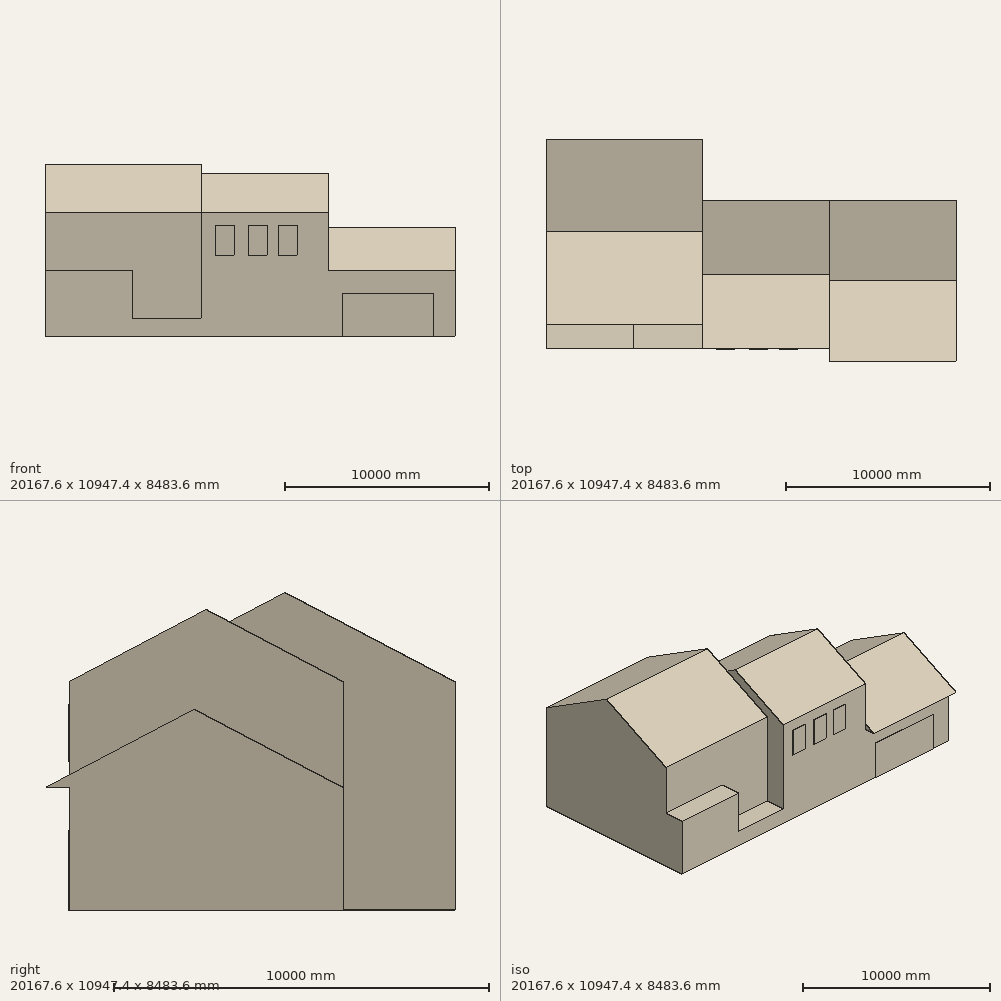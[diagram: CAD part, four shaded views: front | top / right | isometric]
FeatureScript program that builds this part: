
annotation { "Feature Type Name" : "Feature", "Feature Type Description" : "" }
export const myFeature = defineFeature(function(context is Context, id is Id, definition is map)
    precondition{}
    {
        {
            var Q0;
            Q0=qCreatedBy(makeId("Right.planeOp"),FACE);
            cPlane(context, id + "F0", {"entities" : qUnion([Q0]), "cplaneType" : CPlaneType.OFFSET, "offset" : 6248.4 * mm, "width" : 152.4 * mm, "height" : 152.4 * mm});
        }
        {
            var Q0;
            Q0=qCreatedBy(makeId("Right.planeOp"),FACE);
            cPlane(context, id + "F1", {"entities" : qUnion([Q0]), "cplaneType" : CPlaneType.OFFSET, "offset" : 7670.8 * mm, "oppositeDirection" : true, "width" : 152.4 * mm, "height" : 152.4 * mm});
        }
        {
            var Q0;
            Q0=qCreatedBy(id+"F0.planeOp",FACE);
            var sketch = newSketch(context, id + "F2", { "sketchPlane" : qUnion([Q0])});
            skLineSegment(sketch, "E0", {"start": v(0, 0) * mm, "end": v(7315.2, 0) * mm});
            skLineSegment(sketch, "E1.0", {"start": v(7315.2, 0) * mm, "end": v(7315.2, 6.35) * mm});
            skLineSegment(sketch, "E2.MirrorCS", {"start": v(3657.6, 8030.48) * mm, "end": v(7315.2, 6102.35) * mm});
            skLineSegment(sketch, "E3.0", {"start": v(0, 6.35) * mm, "end": v(7315.2, 6.35) * mm});
            skLineSegment(sketch, "E4", {"start": v(0, 6.35) * mm, "end": v(0, 6102.35) * mm});
            skLineSegment(sketch, "E5.trimOffspring", {"start": v(7315.2, 6.35) * mm, "end": v(7315.2, 6102.35) * mm});
            skLineSegment(sketch, "E6.MirrorCS", {"start": v(3657.6, 8030.48) * mm, "end": v(0, 6102.35) * mm});
            skSolve(sketch);
        }
        {
            var Q0;
            Q0=qCreatedBy(makeId("Right.planeOp"),FACE);
            var sketch = newSketch(context, id + "F3", { "sketchPlane" : qUnion([Q0])});
            skLineSegment(sketch, "E7", {"start": v(0, 0) * mm, "end": v(10312.4, 0) * mm});
            skLineSegment(sketch, "E8.0", {"start": v(0, 914.4) * mm, "end": v(1219.2, 914.4) * mm});
            skLineSegment(sketch, "E9.0", {"start": v(1219.2, 914.4) * mm, "end": v(1219.2, 6096) * mm});
            skLineSegment(sketch, "E10.0", {"start": v(10312.4, 0) * mm, "end": v(10312.4, 6096) * mm});
            skLineSegment(sketch, "E11", {"start": v(1219.2, 6096) * mm, "end": v(5765.8, 8483.6) * mm});
            skLineSegment(sketch, "E12", {"start": v(5765.8, 8483.6) * mm, "end": v(10312.4, 6096) * mm});
            skLineSegment(sketch, "E13", {"start": v(0, 0) * mm, "end": v(0, 914.4) * mm});
            skLineSegment(sketch, "E14.0", {"start": v(0, 6.35) * mm, "end": v(10312.4, 6.35) * mm});
            skLineSegment(sketch, "E15.0", {"start": v(0, 12.7) * mm, "end": v(10312.4, 12.7) * mm});
            skSolve(sketch);
        }
        {
            var Q0;
            Q0=qCreatedBy(id+"F1.planeOp",FACE);
            var sketch = newSketch(context, id + "F4", { "sketchPlane" : qUnion([Q0])});
            skLineSegment(sketch, "E16", {"start": v(0, 0) * mm, "end": v(10312.4, 0) * mm});
            skLineSegment(sketch, "E17", {"start": v(0, 0) * mm, "end": v(0, 3276.6) * mm});
            skLineSegment(sketch, "E18.0", {"start": v(10312.4, 0) * mm, "end": v(10312.4, 6096) * mm});
            skLineSegment(sketch, "E19.0", {"start": v(0, 3276.6) * mm, "end": v(1219.2, 3276.6) * mm});
            skLineSegment(sketch, "E20.0", {"start": v(1219.2, 3276.6) * mm, "end": v(1219.2, 6096) * mm});
            skLineSegment(sketch, "E21", {"start": v(1219.2, 6096) * mm, "end": v(5765.8, 8483.6) * mm});
            skLineSegment(sketch, "E22", {"start": v(10312.4, 6096) * mm, "end": v(5765.8, 8483.6) * mm});
            skSolve(sketch);
        }
        {
            var Q0;
            Q0=qCreatedBy(makeId("Right.planeOp"),FACE);
            cPlane(context, id + "F5", {"entities" : qUnion([Q0]), "cplaneType" : CPlaneType.OFFSET, "offset" : 6705.6 * mm, "width" : 152.4 * mm, "height" : 152.4 * mm});
        }
        {
            var Q0;
            Q0=qCreatedBy(makeId("Right.planeOp"),FACE);
            cPlane(context, id + "F6", {"entities" : qUnion([Q0]), "cplaneType" : CPlaneType.OFFSET, "offset" : 8128 * mm, "oppositeDirection" : true, "width" : 152.4 * mm, "height" : 152.4 * mm});
        }
        {
            var Q0;
            Q0=makeQuery(id+"F4.imprint","IMPRINT",FACE,{"disambiguationData":[TD([[makeQuery(id+"F4.imprint","IMPRINT",EDGE,{"derivedFrom":sQuery(id+"F4.wireOp",EDGE,"E16")}),1.0]])]});
            extrude(context, id + "F7", {"entities" : qUnion([Q0]), "depth" : 4267.2 * mm});
        }
        {
            var Q0;
            {var subQ0=sQuery(id+"F3.wireOp",EDGE,"E8.0");Q0=makeQuery(id+"F3.imprint","IMPRINT",FACE,{"disambiguationData":[TD([[makeQuery(id+"F3.imprint","IMPRINT",EDGE,{"derivedFrom":subQ0}),-1.0]])]});}
            extrude(context, id + "F8", {"entities" : qUnion([Q0]), "operationType" : NewBodyOperationType.ADD, "oppositeDirection" : true, "depth" : 3403.6 * mm});
        }
        {
            var Q0;
            Q0=makeQuery(id+"F2.imprint","IMPRINT",FACE,{"disambiguationData":[TD([[makeQuery(id+"F2.imprint","IMPRINT",EDGE,{"derivedFrom":sQuery(id+"F2.wireOp",EDGE,"E2.MirrorCS")}),-1.0]])]});
            extrude(context, id + "F9", {"entities" : qUnion([Q0]), "operationType" : NewBodyOperationType.ADD, "oppositeDirection" : true, "depth" : 6248.4 * mm});
        }
        {
            var Q0;
            Q0=qCreatedBy(id+"F0.planeOp",FACE);
            cPlane(context, id + "F10", {"entities" : qUnion([Q0]), "cplaneType" : CPlaneType.OFFSET, "offset" : 6248.4 * mm, "width" : 152.4 * mm, "height" : 152.4 * mm});
        }
        {
            var Q0;
            Q0=qCreatedBy(id+"F10.planeOp",FACE);
            var sketch = newSketch(context, id + "F11", { "sketchPlane" : qUnion([Q0])});
            skLineSegment(sketch, "E23", {"start": v(0, 0) * mm, "end": v(7315.2, 0) * mm});
            skLineSegment(sketch, "E24", {"start": v(0, 3270.25) * mm, "end": v(0, 0) * mm});
            skLineSegment(sketch, "E25", {"start": v(7315.2, 3276.6) * mm, "end": v(7315.2, 0) * mm});
            skLineSegment(sketch, "E26", {"start": v(-635, 3276.6) * mm, "end": v(0, 3270.25) * mm});
            skLineSegment(sketch, "E27", {"start": v(-635, 3276.6) * mm, "end": v(3340.1, 5365.75) * mm});
            skLineSegment(sketch, "E28", {"start": v(3340.1, 5365.75) * mm, "end": v(7315.2, 3276.6) * mm});
            skSolve(sketch);
        }
        {
            var Q0;
            Q0 = qSketchRegion(id + "F11", true);
            extrude(context, id + "F12", {"entities" : qUnion([Q0]), "operationType" : NewBodyOperationType.ADD, "oppositeDirection" : true, "depth" : 6248.4 * mm});
        }
        {
            var Q0;
            Q0=makeQuery(id+"F12.boolean.opBoolean","MERGE",FACE,{"derivedFrom":[makeQuery(id+"F9.boolean.opBoolean","MERGE",FACE,{"derivedFrom":[makeQuery(id+"F8.boolean.opBoolean","MERGE",FACE,{"derivedFrom":[makeQuery(id+"F7.opExtrude","SWEPT_FACE",FACE,{"disambiguationData":[OSD([sQuery(id+"F4.wireOp",EDGE,"E17")])]}),makeQuery(id+"F8.opExtrude","SWEPT_FACE",FACE,{"disambiguationData":[OSD([sQuery(id+"F3.wireOp",EDGE,"E13")])]})]}),makeQuery(id+"F9.opExtrude","SWEPT_FACE",FACE,{"disambiguationData":[OSD([sQuery(id+"F2.wireOp",EDGE,"E4")])]})]}),makeQuery(id+"F12.opExtrude","SWEPT_FACE",FACE,{"disambiguationData":[OSD([sQuery(id+"F11.wireOp",EDGE,"E24")])]})]});
            var sketch = newSketch(context, id + "F13", { "sketchPlane" : qUnion([Q0])});
            skLineSegment(sketch, "E29.0", {"start": v(5254.96, 6425.77) * mm, "end": v(5254.96, 8558.64) * mm});
            skLineSegment(sketch, "E30.0", {"start": v(5353.05, 12.7) * mm, "end": v(5353.05, 2142.05) * mm});
            skLineSegment(sketch, "E31.0", {"start": v(1.7, 2146.3) * mm, "end": v(19.05, 2146.29) * mm});
            skLineSegment(sketch, "E32.trimOffspring", {"start": v(914.4, 2145.58) * mm, "end": v(5353.05, 2142.05) * mm});
            skLineSegment(sketch, "E33", {"start": v(914.4, 12.7) * mm, "end": v(5353.05, 12.7) * mm});
            skLineSegment(sketch, "E34.0", {"start": v(6952.01, 0) * mm, "end": v(6952.01, 2132.88) * mm});
            skLineSegment(sketch, "E35.0", {"start": v(11390.66, 0) * mm, "end": v(11390.66, 2129.35) * mm});
            skLineSegment(sketch, "E36.trimOffspring", {"start": v(6952.01, 2132.88) * mm, "end": v(11390.66, 2129.35) * mm});
            skLineSegment(sketch, "E37", {"start": v(6952.01, 0) * mm, "end": v(11390.66, 0) * mm});
            skLineSegment(sketch, "E38.bottom", {"start": v(702.16, 5493.21) * mm, "end": v(1621.6, 5493.21) * mm});
            skLineSegment(sketch, "E38.top", {"start": v(5042.72, 10389.21) * mm, "end": v(5962.15, 10389.21) * mm});
            skLineSegment(sketch, "E38.left", {"start": v(702.16, 5493.21) * mm, "end": v(702.16, 3976.14) * mm});
            skLineSegment(sketch, "E38.right", {"start": v(1621.6, 5493.21) * mm, "end": v(1621.6, 3976.14) * mm});
            skLineSegment(sketch, "E39.bottom", {"start": v(2307.4, 5493.21) * mm, "end": v(3226.83, 5493.21) * mm});
            skLineSegment(sketch, "E39.top", {"start": v(2307.4, 3976.14) * mm, "end": v(3226.83, 3976.14) * mm});
            skLineSegment(sketch, "E39.left", {"start": v(2307.4, 5493.21) * mm, "end": v(2307.4, 3976.14) * mm});
            skLineSegment(sketch, "E39.right", {"start": v(3226.83, 5493.21) * mm, "end": v(3226.83, 3976.14) * mm});
            skLineSegment(sketch, "E40", {"start": v(702.16, 3976.14) * mm, "end": v(1621.6, 3976.14) * mm});
            skLineSegment(sketch, "E41.bottom", {"start": v(3799.17, 5493.21) * mm, "end": v(4718.6, 5493.21) * mm});
            skLineSegment(sketch, "E41.top", {"start": v(3799.17, 3976.14) * mm, "end": v(4718.6, 3976.14) * mm});
            skLineSegment(sketch, "E41.left", {"start": v(3799.17, 5493.21) * mm, "end": v(3799.17, 3976.14) * mm});
            skLineSegment(sketch, "E41.right", {"start": v(4718.6, 5493.21) * mm, "end": v(4718.6, 3976.14) * mm});
            skSolve(sketch);
        }
        {
            var Q0;
            Q0 = qSketchRegion(id + "F13", true);
            extrude(context, id + "F14", {"entities" : qUnion([Q0]), "operationType" : NewBodyOperationType.ADD, "depth" : 25.4 * mm});
        }
    });
